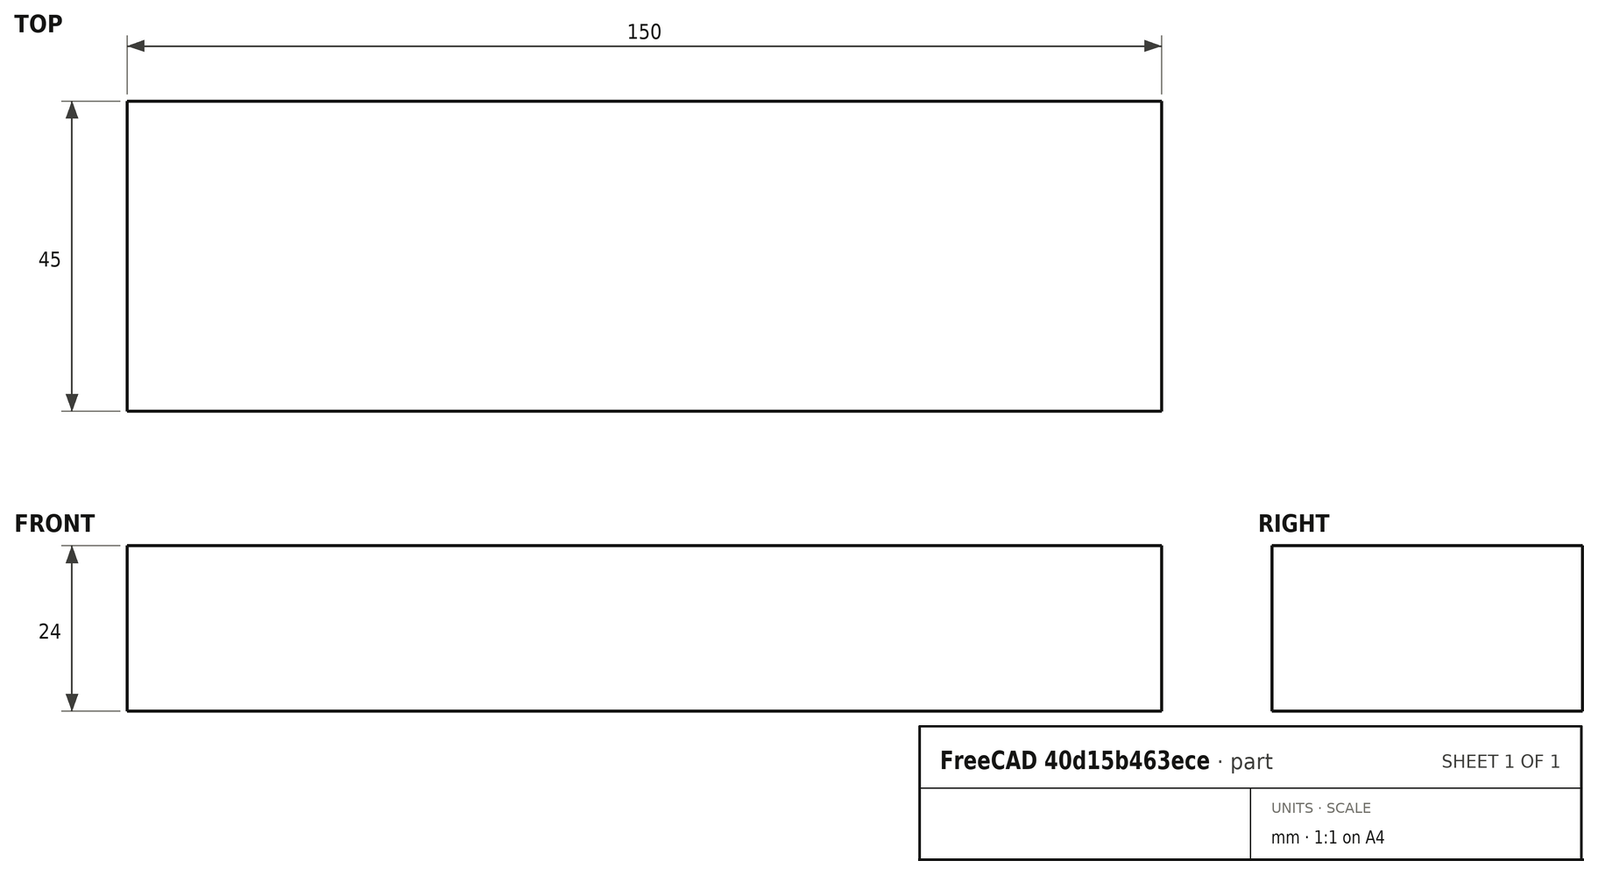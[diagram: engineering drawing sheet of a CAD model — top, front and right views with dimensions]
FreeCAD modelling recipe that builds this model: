
FCSTD DOCUMENT  (FreeCAD 1.0R39109 (Git))
Label: battery
License: All rights reserved
LicenseURL: https://en.wikipedia.org/wiki/All_rights_reserved
objects: Sketcher::SketchObject×1, PartDesign::Pad×1, PartDesign::Body×1
note: 6 computed .brp shape members not serialized (recipe doc carries the construction recipe); baked Part::Feature solids carry a one-line shape summary decoded from their .brp

FEATURE [Sketcher::SketchObject] Sketch
  ArcFitTolerance = 1e-06
  AttachmentSupport = -> [XY_Plane]
  FullyConstrained = true
  MakeInternals = false
  MapMode = 5
  sketch-geometry (4):
    g0: LineSegment StartX=-75 StartY=22.5 StartZ=0 EndX=-75 EndY=-22.5 EndZ=0
    g1: LineSegment StartX=-75 StartY=-22.5 StartZ=0 EndX=75 EndY=-22.5 EndZ=0
    g2: LineSegment StartX=75 StartY=-22.5 StartZ=0 EndX=75 EndY=22.5 EndZ=0
    g3: LineSegment StartX=75 StartY=22.5 StartZ=0 EndX=-75 EndY=22.5 EndZ=0
  constraints (12):
    c: Coincident(g0,g1)
    c: Coincident(g1,g2)
    c: Coincident(g2,g3)
    c: Coincident(g3,g0)
    c: Vertical(g0)
    c: Vertical(g2)
    c: Horizontal(g1)
    c: Horizontal(g3)
    c: DistanceX(g3,g3) = 150
    c: DistanceY(g2,g2) = 45
    c: Distance(g-1,g3) = 22.5
    c: Distance(g-2,g0) = 75
FEATURE [PartDesign::Pad] Pad
  Direction = (0,0,1)
  Length = 24
  Length2 = 10
  Profile = -> Sketch
  ReferenceAxis = -> Sketch [N_Axis]
  Refine = true
  Suppressed = false
  Type = 0
FEATURE [PartDesign::Body] Body
  AllowCompound = false
  Group = -> [Sketch,Pad]
  Origin = -> Origin
  Tip = -> Pad
